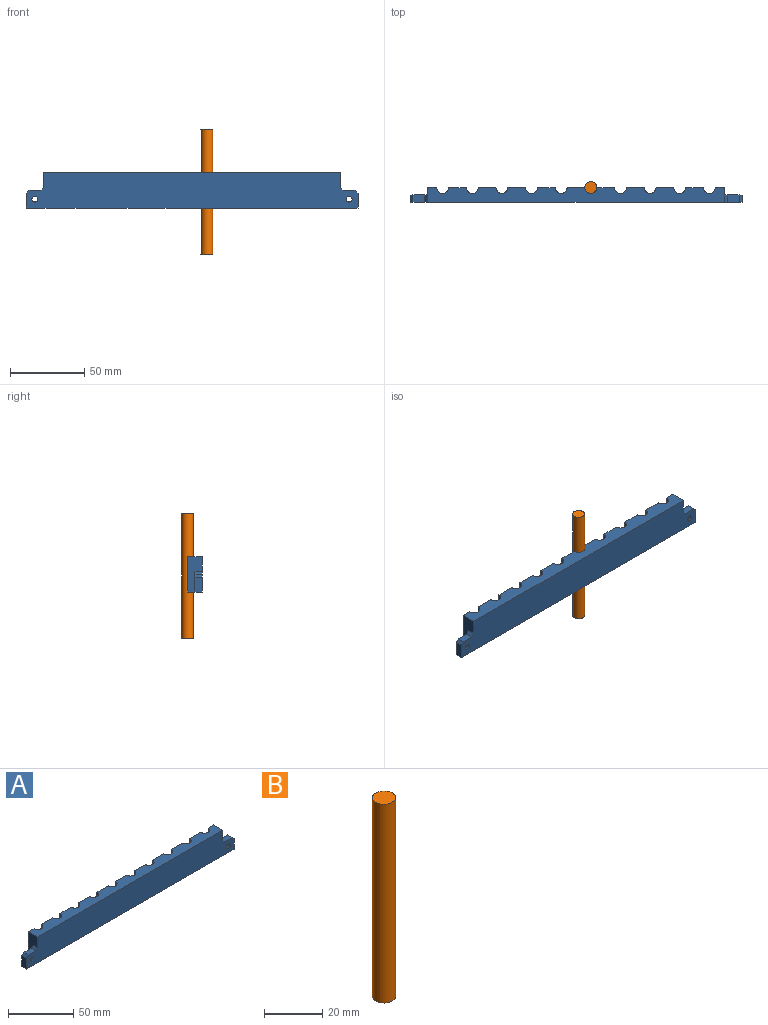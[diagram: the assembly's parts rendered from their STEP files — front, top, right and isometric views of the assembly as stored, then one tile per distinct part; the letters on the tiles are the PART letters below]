
ASSEMBLY  parts=2 mates=1
PART A: 80 faces, bbox 224x10x23.9 mm
  f0: plane 23.9x10mm, normal (-1,0,0), area 169mm2, adj f2,f6,f8,f10,f69,f76
  f1: cylinder r=4mm len=23.9mm, axis (0,0,-1), area 300.3mm2, adj f2,f4,f8,f10
  f2: plane 23.9x6mm, normal (0,1,0), area 83.7mm2, adj f0,f1,f3,f5,f7,f8,f9,f10
  f3: cylinder r=6mm len=19.9mm, axis (0,0,-1), area 375.1mm2, adj f2,f4,f7,f9
  f4: plane 23.9x12mm, normal (0,1,0), area 167.4mm2, adj f1,f3,f5,f7,f8,f9,f10,f11
  f5: cylinder r=9mm len=19.9mm, axis (0,0,-1), area 562.7mm2, adj f2,f4,f7,f9
  f6: plane 224x23.9mm, normal (0,-1,0), area 5042.9mm2, adj f0,f8,f10,f58,f66,f67,f68,f70
  f7: plane 18x9mm, normal (0,0,-1), area 70.7mm2, adj f2,f3,f4,f5
  f8: plane 200x10mm, normal (0,0,1), area 1748.7mm2, adj f0,f1,f2,f4,f6,f11,f13,f17
  f9: plane 18x9mm, normal (0,0,1), area 70.7mm2, adj f2,f3,f4,f5
  f10: plane 224x10mm, normal (0,0,-1), area 1868.7mm2, adj f0,f1,f2,f4,f6,f11,f13,f17
  f11: cylinder r=4mm len=23.9mm, axis (0,0,-1), area 300.3mm2, adj f4,f8,f10,f13
  f12: cylinder r=6mm len=19.9mm, axis (0,0,-1), area 375.1mm2, adj f4,f13,f15,f16
  f13: plane 23.9x12mm, normal (0,1,0), area 167.4mm2, adj f8,f10,f11,f12,f14,f15,f16,f17
  f14: cylinder r=9mm len=19.9mm, axis (0,0,-1), area 562.7mm2, adj f4,f13,f15,f16
  f15: plane 18x9mm, normal (0,0,-1), area 70.7mm2, adj f4,f12,f13,f14
  f16: plane 18x9mm, normal (0,0,1), area 70.7mm2, adj f4,f12,f13,f14
  f17: cylinder r=4mm len=23.9mm, axis (0,0,-1), area 300.3mm2, adj f8,f10,f13,f19
  f18: cylinder r=6mm len=19.9mm, axis (0,0,-1), area 375.1mm2, adj f13,f19,f21,f22
  f19: plane 23.9x12mm, normal (0,1,0), area 167.4mm2, adj f8,f10,f17,f18,f20,f21,f22,f61
  f20: cylinder r=9mm len=19.9mm, axis (0,0,-1), area 562.7mm2, adj f13,f19,f21,f22
  f21: plane 18x9mm, normal (0,0,-1), area 70.7mm2, adj f13,f18,f19,f20
  f22: plane 18x9mm, normal (0,0,1), area 70.7mm2, adj f13,f18,f19,f20
  f23: cylinder r=4mm len=23.9mm, axis (0,0,-1), area 300.3mm2, adj f8,f10,f24,f26
  f24: plane 23.9x12mm, normal (0,1,0), area 167.4mm2, adj f8,f10,f23,f25,f27,f28,f29,f61
  f25: cylinder r=6mm len=19.9mm, axis (0,0,-1), area 375.1mm2, adj f24,f26,f28,f29
  f26: plane 23.9x12mm, normal (0,1,0), area 167.4mm2, adj f8,f10,f23,f25,f27,f28,f29,f30
  f27: cylinder r=9mm len=19.9mm, axis (0,0,-1), area 562.7mm2, adj f24,f26,f28,f29
  f28: plane 18x9mm, normal (0,0,-1), area 70.7mm2, adj f24,f25,f26,f27
  f29: plane 18x9mm, normal (0,0,1), area 70.7mm2, adj f24,f25,f26,f27
  f30: cylinder r=4mm len=23.9mm, axis (0,0,-1), area 300.3mm2, adj f8,f10,f26,f32
  f31: cylinder r=6mm len=19.9mm, axis (0,0,-1), area 375.1mm2, adj f26,f32,f34,f35
  f32: plane 23.9x12mm, normal (0,1,0), area 167.4mm2, adj f8,f10,f30,f31,f33,f34,f35,f36
  f33: cylinder r=9mm len=19.9mm, axis (0,0,-1), area 562.7mm2, adj f26,f32,f34,f35
  f34: plane 18x9mm, normal (0,0,-1), area 70.7mm2, adj f26,f31,f32,f33
  f35: plane 18x9mm, normal (0,0,1), area 70.7mm2, adj f26,f31,f32,f33
  f36: cylinder r=4mm len=23.9mm, axis (0,0,-1), area 300.3mm2, adj f8,f10,f32,f38
  f37: cylinder r=6mm len=19.9mm, axis (0,0,-1), area 375.1mm2, adj f32,f38,f40,f41
  f38: plane 23.9x12mm, normal (0,1,0), area 167.4mm2, adj f8,f10,f36,f37,f39,f40,f41,f42
  f39: cylinder r=9mm len=19.9mm, axis (0,0,-1), area 562.7mm2, adj f32,f38,f40,f41
  f40: plane 18x9mm, normal (0,0,-1), area 70.7mm2, adj f32,f37,f38,f39
  f41: plane 18x9mm, normal (0,0,1), area 70.7mm2, adj f32,f37,f38,f39
  f42: cylinder r=4mm len=23.9mm, axis (0,0,-1), area 300.3mm2, adj f8,f10,f38,f44
  f43: cylinder r=6mm len=19.9mm, axis (0,0,-1), area 375.1mm2, adj f38,f44,f46,f47
  f44: plane 23.9x12mm, normal (0,1,0), area 167.4mm2, adj f8,f10,f42,f43,f45,f46,f47,f48
  f45: cylinder r=9mm len=19.9mm, axis (0,0,-1), area 562.7mm2, adj f38,f44,f46,f47
  f46: plane 18x9mm, normal (0,0,-1), area 70.7mm2, adj f38,f43,f44,f45
  f47: plane 18x9mm, normal (0,0,1), area 70.7mm2, adj f38,f43,f44,f45
  f48: cylinder r=4mm len=23.9mm, axis (0,0,-1), area 300.3mm2, adj f8,f10,f44,f50
  f49: cylinder r=6mm len=19.9mm, axis (0,0,-1), area 375.1mm2, adj f44,f50,f52,f53
  f50: plane 23.9x12mm, normal (0,1,0), area 167.4mm2, adj f8,f10,f48,f49,f51,f52,f53,f54
  f51: cylinder r=9mm len=19.9mm, axis (0,0,-1), area 562.7mm2, adj f44,f50,f52,f53
  f52: plane 18x9mm, normal (0,0,-1), area 70.7mm2, adj f44,f49,f50,f51
  f53: plane 18x9mm, normal (0,0,1), area 70.7mm2, adj f44,f49,f50,f51
  f54: cylinder r=4mm len=23.9mm, axis (0,0,-1), area 300.3mm2, adj f8,f10,f50,f56
  f55: cylinder r=6mm len=19.9mm, axis (0,0,-1), area 375.1mm2, adj f50,f56,f59,f60
  f56: plane 23.9x6mm, normal (0,1,0), area 83.7mm2, adj f8,f10,f54,f55,f57,f58,f59,f60
  f57: cylinder r=9mm len=19.9mm, axis (0,0,-1), area 562.7mm2, adj f50,f56,f59,f60
  f58: plane 23.9x10mm, normal (1,0,0), area 169mm2, adj f6,f8,f10,f56,f73,f78
  f59: plane 18x9mm, normal (0,0,-1), area 70.7mm2, adj f50,f55,f56,f57
  f60: plane 18x9mm, normal (0,0,1), area 70.7mm2, adj f50,f55,f56,f57
  f61: cylinder r=4mm len=23.9mm, axis (0,0,-1), area 300.3mm2, adj f8,f10,f19,f24
  f62: cylinder r=6mm len=19.9mm, axis (0,0,-1), area 375.1mm2, adj f19,f24,f64,f65
  f63: cylinder r=9mm len=19.9mm, axis (0,0,-1), area 562.7mm2, adj f19,f24,f64,f65
  f64: plane 18x9mm, normal (0,0,-1), area 70.7mm2, adj f19,f24,f62,f63
  f65: plane 18x9mm, normal (0,0,1), area 70.7mm2, adj f19,f24,f62,f63
  f66: plane 8x5mm, normal (0,0,1), area 40mm2, adj f6,f69,f76,f77
  f67: plane 10x5mm, normal (-1,0,0), area 50mm2, adj f6,f10,f69,f77
  f68: cylinder r=2mm len=4mm, axis (0,-1,0), area 25.1mm2, adj f6,f74
  f69: plane 14x12mm, normal (0,1,0), area 65.5mm2, adj f0,f10,f66,f67,f74,f76,f77
  f70: plane 10x5mm, normal (1,0,0), area 50mm2, adj f6,f10,f73,f79
  f71: plane 8x5mm, normal (0,0,1), area 40mm2, adj f6,f73,f78,f79
  f72: cylinder r=2mm len=4mm, axis (0,-1,0), area 25.1mm2, adj f6,f75
  f73: plane 14x12mm, normal (0,1,0), area 65.5mm2, adj f10,f58,f70,f71,f75,f78,f79
  f74: cone r=5mm half-angle=45deg, axis (0,1,0), area 93.3mm2, adj f68,f69
  f75: cone r=2mm half-angle=45deg, axis (0,1,0), area 93.3mm2, adj f72,f73
  f76: plane 5x2mm, normal (-0.71,0,0.71), area 14.1mm2, adj f0,f6,f66,f69
  f77: plane 5x2mm, normal (-0.71,0,0.71), area 14.1mm2, adj f6,f66,f67,f69
  f78: plane 5x2mm, normal (0.71,0,0.71), area 14.1mm2, adj f6,f58,f71,f73
  f79: plane 5x2mm, normal (0.71,0,0.71), area 14.1mm2, adj f6,f70,f71,f73
PART B: 3 faces, bbox 8x8x83.8 mm
  f0: cylinder r=4mm len=83.8mm, axis (0,0,-1), area 2106.1mm2, adj f1,f2
  f1: plane 8x8mm, normal (0,0,1), area 50.3mm2, adj f0
  f2: plane 8x8mm, normal (0,0,-1), area 50.3mm2, adj f0
PLACE A t=(-42.39,1.98,-5.36)mm fixed
PLACE B t=(12.56,39.39,-38.46)mm
MATE slider B.f0 <-> A.f30  axis (0,0,-1) through (12.56,39.39,3.44)mm
